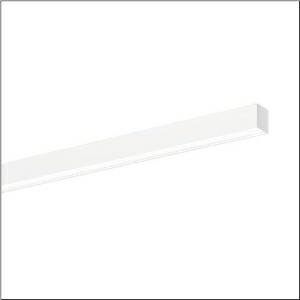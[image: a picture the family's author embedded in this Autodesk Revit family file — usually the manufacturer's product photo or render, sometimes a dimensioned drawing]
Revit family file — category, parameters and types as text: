
# Revit family: silica_r__21_51mx23db45wb_81de
name_source: partatom
category: Lighting Fixtures
units: mm (PartAtom-declared; Revit-internal decimal feet)

## family parameters
Cut with Voids When Loaded = No
Host = Face
Light Source = No
Part Type = Normal
Room Calculation Point = No
Round Connector Dimension = Use Diameter
Shared = No

## types (1)
- --- (1 x LED, 4100 lm, 28.1 W, 4000K)
    Apparent Load = 28 VA
    CIE Flux Codes = 78 96 99 100 100
    Color Rendering = 80
    Color Temperature = 4000K
    Default Elevation = 1800 mm
    Description = Silica® 21, office luminaire, primary optical cover: prismatic diffuser, of PMMA, CAT 2 (L<= 3000cd/m²), light emission: direct distribution, primary light characteristic: symmetric, installation type: surface-mounted, LED, rated luminous flux: 4.100lm, luminous efficacy: 146lm/W, light colour: 840, colour temperature: 4000K, control gear: DALI 2, with terminal, 3+2-pole, max. 2.5mm², mains connection: 220..240V, AC, 50/60Hz, rated input power: 28.1W, luminaire housing, of aluminium, traffic white (RAL 9016), length: 1.504mm, width: 53mm, height: 53mm, protection rating (complete): IP20, insulation class (complete): insulation class I (protective earthing), certification: CE, permissible operating ambient temperature: 0..+35°C, standard: EN 50419, packaging unit: 1 piece
    Height = 53 mm
    Lamp = 1 x LED
    Lamp Light Flux = 4100 lm
    Lamp Power = 28.1 W
    Lamp count = 1
    Length = 1504 mm
    Luminous efficacy = 146 lm/W
    Manufacturer = Siteco
    ModVariant = No
    Model = 51MX23DB45WB
    Mounting Place = Ceiling
    Mounting Type = Surface mounted
    Number of Poles = 1
    OnlyDefault = Yes
    Power Factor = 1
    Product Name = Silica® 21
    Product group = office luminaire | ceiling mounted
    ProductGroupID = 303
    Protection Class = Protection class I
    Protection Degree = IP 20
    RLX_Detail_Level = 1
    RLX_Emergency_Light_Flux = 0 lm
    RLX_Emergency_Type = 0
    RLX_Emergency_Type_DB = No
    RlxData = <blob elided: 18845 chars, md5=ed047029>
    Socket = socket
    Standby Power = 0 W
    System Light Flux = 4100 lm
    System Power = 28 W
    Type Comments = factory setting: luminous flux: 100 % | dim-lin: 254 | 323 mA
    Type Image = l_1335877.jpg
    URL = http://relux.com
    VarID = @adj_141111
    Voltage = 0 V
    Weight = 0.00 kg
    Width = 53 mm

## geometry (parser evidence)
native form markers: Blend x4, Sweep x12
no freeform markers — native parametric forms only
